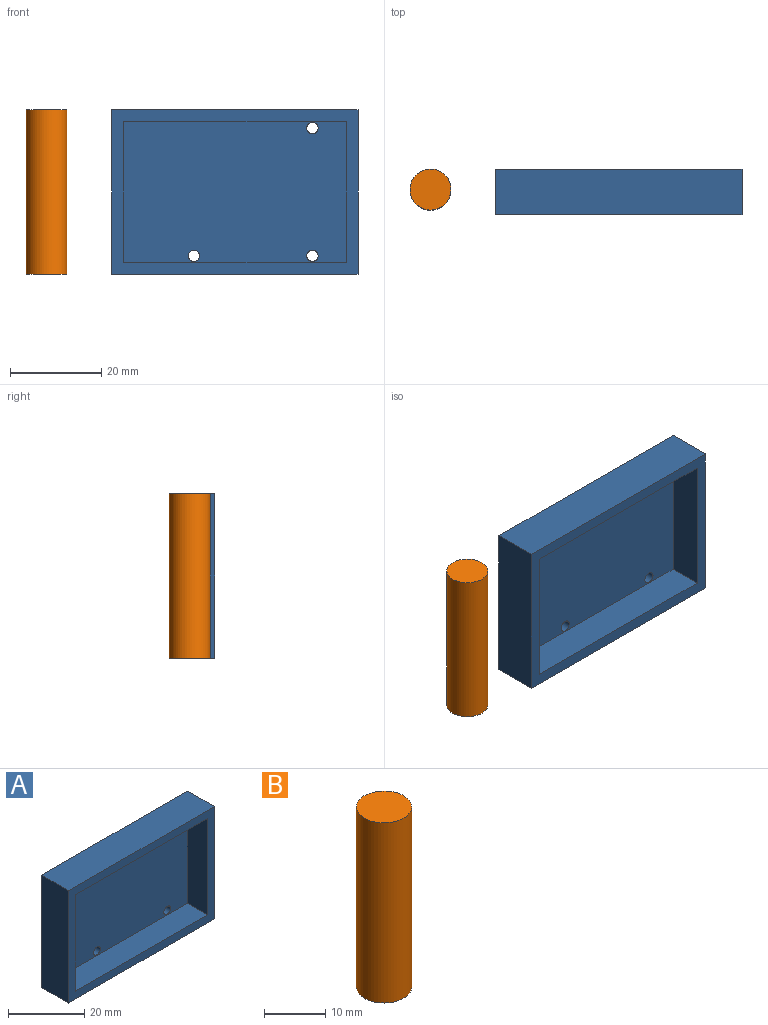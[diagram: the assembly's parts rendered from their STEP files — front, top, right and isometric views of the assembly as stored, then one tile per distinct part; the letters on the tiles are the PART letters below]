
ASSEMBLY  parts=2 mates=1
PART A: 14 faces, bbox 54x10x36 mm
  f0: plane 54x36mm, normal (0,-1,0), area 431.4mm2, adj f1,f2,f3,f4,f6,f7,f8,f9
  f1: plane 54x10mm, normal (0,0,1), area 540mm2, adj f0,f2,f4,f5
  f2: plane 36x10mm, normal (-1,0,0), area 360mm2, adj f0,f1,f3,f5
  f3: plane 54x10mm, normal (0,0,-1), area 540mm2, adj f0,f2,f4,f5
  f4: plane 36x10mm, normal (1,0,0), area 360mm2, adj f0,f1,f3,f5
  f5: plane 54x36mm, normal (0,1,0), area 1929.3mm2, adj f1,f2,f3,f4,f11,f12,f13
  f6: plane 48.92x7.46mm, normal (0,0,-1), area 364.9mm2, adj f0,f7,f9,f10
  f7: plane 30.92x7.46mm, normal (1,0,0), area 230.7mm2, adj f0,f6,f8,f10
  f8: plane 48.92x7.46mm, normal (0,0,1), area 364.9mm2, adj f0,f7,f9,f10
  f9: plane 30.92x7.46mm, normal (-1,0,0), area 230.7mm2, adj f0,f6,f8,f10
  f10: plane 48.92x30.92mm, normal (0,-1,0), area 1497.9mm2, adj f6,f7,f8,f9,f11,f12,f13
  f11: cylinder r=1.25mm len=2.54mm, axis (0,1,0), area 19.9mm2, adj f5,f10
  f12: cylinder r=1.25mm len=2.54mm, axis (0,1,0), area 19.9mm2, adj f5,f10
  f13: cylinder r=1.25mm len=2.54mm, axis (0,1,0), area 19.9mm2, adj f5,f10
PART B: 3 faces, bbox 9x9x36 mm
  f0: plane 9x9mm, normal (0,0,1), area 63.6mm2, adj f1
  f1: cylinder r=4.5mm len=36mm, axis (0,0,-1), area 1017.9mm2, adj f0,f2
  f2: plane 9x9mm, normal (0,0,-1), area 63.6mm2, adj f1
PLACE A t=(-26.94,0,-20.31)mm
PLACE B rot(axis=(0,0,-1),81.7deg) t=(-45.28,54.04,-20.31)mm
MATE planar A.f1 <-> B.f1  axis (0,0,1) through (0.06,-10,15.69)mm
